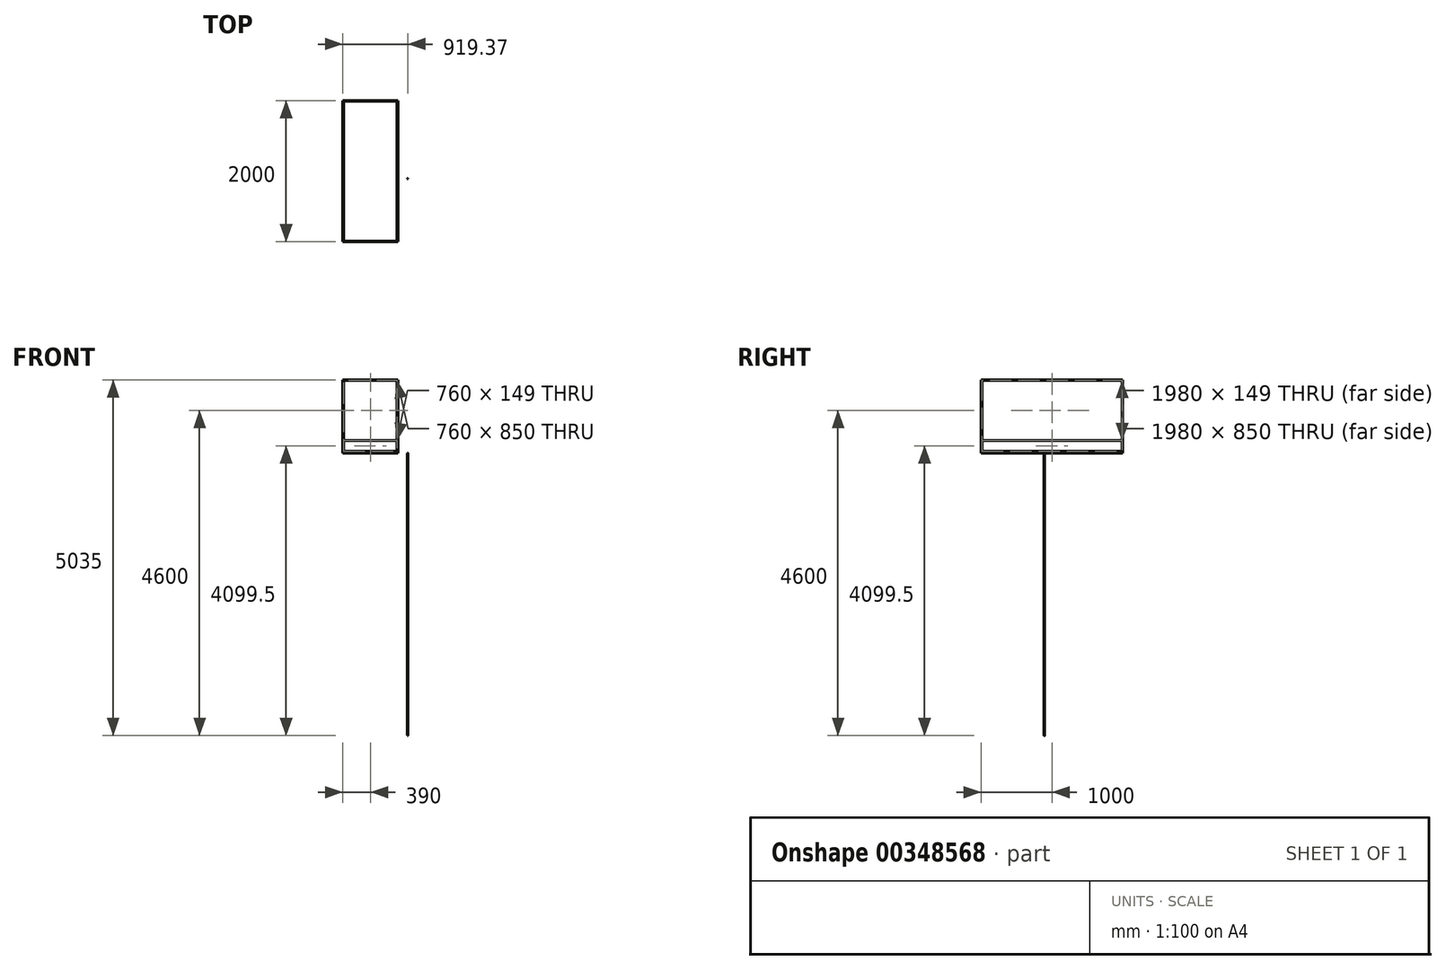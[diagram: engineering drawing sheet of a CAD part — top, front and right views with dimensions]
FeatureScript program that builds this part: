
annotation { "Feature Type Name" : "Feature", "Feature Type Description" : "" }
export const myFeature = defineFeature(function(context is Context, id is Id, definition is map)
    precondition{}
    {
        {
            var Q0;
            Q0=qCreatedBy(makeId("Top.planeOp"),FACE);
            var sketch = newSketch(context, id + "F0", { "sketchPlane" : qUnion([Q0])});
            skLineSegment(sketch, "E0.rect.bottom", {"start": v(390, -1000) * mm, "end": v(-390, -1000) * mm});
            skLineSegment(sketch, "E0.rect.top", {"start": v(390, 1000) * mm, "end": v(-390, 1000) * mm});
            skLineSegment(sketch, "E0.rect.left", {"start": v(390, -1000) * mm, "end": v(390, 1000) * mm});
            skLineSegment(sketch, "E0.rect.right", {"start": v(-390, -1000) * mm, "end": v(-390, 1000) * mm});
            skPoint(sketch, "E0.rect.middle", {"position": v(0, 0) * mm});
            skSolve(sketch);
        }
        {
            var Q0;
            Q0=makeQuery(id+"F0.imprint","IMPRINT",FACE,{"disambiguationData":[TD([[makeQuery(id+"F0.imprint","IMPRINT",EDGE,{"derivedFrom":sQuery(id+"F0.wireOp",EDGE,"E0.rect.bottom")}),-1.0]])]});
            extrude(context, id + "F1", {"entities" : qUnion([Q0]), "depth" : 25 * mm});
        }
        {
            var Q0;
            Q0=makeQuery(id+"F1.opExtrude","CAP_FACE",FACE,{"disambiguationData":[OSD([sQuery(id+"F0.wireOp",EDGE,"E0.rect.bottom"),sQuery(id+"F0.wireOp",EDGE,"E0.rect.top"),sQuery(id+"F0.wireOp",EDGE,"E0.rect.left"),sQuery(id+"F0.wireOp",EDGE,"E0.rect.right")])],"isStart":false});
            var sketch = newSketch(context, id + "F2", { "sketchPlane" : qUnion([Q0])});
            skLineSegment(sketch, "E1.bottom", {"start": v(-390, -1000) * mm, "end": v(-380, -1000) * mm});
            skLineSegment(sketch, "E1.top", {"start": v(-390, -990) * mm, "end": v(-380, -990) * mm});
            skLineSegment(sketch, "E1.left", {"start": v(-390, -1000) * mm, "end": v(-390, -990) * mm});
            skLineSegment(sketch, "E1.right", {"start": v(-380, -1000) * mm, "end": v(-380, -990) * mm});
            skLineSegment(sketch, "E2.bottom", {"start": v(390, -1000) * mm, "end": v(380, -1000) * mm});
            skLineSegment(sketch, "E2.top", {"start": v(390, -990) * mm, "end": v(380, -990) * mm});
            skLineSegment(sketch, "E2.left", {"start": v(390, -1000) * mm, "end": v(390, -990) * mm});
            skLineSegment(sketch, "E2.right", {"start": v(380, -1000) * mm, "end": v(380, -990) * mm});
            skLineSegment(sketch, "E3.bottom", {"start": v(390, 1000) * mm, "end": v(380, 1000) * mm});
            skLineSegment(sketch, "E3.top", {"start": v(390, 990) * mm, "end": v(380, 990) * mm});
            skLineSegment(sketch, "E3.left", {"start": v(390, 1000) * mm, "end": v(390, 990) * mm});
            skLineSegment(sketch, "E3.right", {"start": v(380, 1000) * mm, "end": v(380, 990) * mm});
            skLineSegment(sketch, "E4.bottom", {"start": v(-390, 1000) * mm, "end": v(-380, 1000) * mm});
            skLineSegment(sketch, "E4.top", {"start": v(-390, 990) * mm, "end": v(-380, 990) * mm});
            skLineSegment(sketch, "E4.left", {"start": v(-390, 1000) * mm, "end": v(-390, 990) * mm});
            skLineSegment(sketch, "E4.right", {"start": v(-380, 1000) * mm, "end": v(-380, 990) * mm});
            skSolve(sketch);
        }
        {
            var Q0;
            Q0=qSketchRegion(id+"F2",true);
            extrude(context, id + "F3", {"entities" : qUnion([Q0]), "operationType" : NewBodyOperationType.ADD, "depth" : 1000 * mm});
        }
        {
            var Q0;
            Q0=makeQuery(id+"F3.opExtrude","CAP_FACE",FACE,{"disambiguationData":[OSD([sQuery(id+"F2.wireOp",EDGE,"E1.bottom"),sQuery(id+"F2.wireOp",EDGE,"E1.top"),sQuery(id+"F2.wireOp",EDGE,"E1.left"),sQuery(id+"F2.wireOp",EDGE,"E1.right")])],"isStart":false});
            var sketch = newSketch(context, id + "F4", { "sketchPlane" : qUnion([Q0])});
            skLineSegment(sketch, "E5.bottom", {"start": v(-390, -1000) * mm, "end": v(-380, -1000) * mm});
            skLineSegment(sketch, "E5.top", {"start": v(-390, 1000) * mm, "end": v(-380, 1000) * mm});
            skLineSegment(sketch, "E5.left", {"start": v(-390, -1000) * mm, "end": v(-390, 1000) * mm});
            skLineSegment(sketch, "E5.right", {"start": v(-380, -1000) * mm, "end": v(-380, 1000) * mm});
            skLineSegment(sketch, "E6.bottom", {"start": v(390, -1000) * mm, "end": v(380, -1000) * mm});
            skLineSegment(sketch, "E6.top", {"start": v(390, 1000) * mm, "end": v(380, 1000) * mm});
            skLineSegment(sketch, "E6.left", {"start": v(390, -1000) * mm, "end": v(390, 1000) * mm});
            skLineSegment(sketch, "E6.right", {"start": v(380, -1000) * mm, "end": v(380, 1000) * mm});
            skLineSegment(sketch, "E7.bottom", {"start": v(380, 1000) * mm, "end": v(-380, 1000) * mm});
            skLineSegment(sketch, "E7.top", {"start": v(380, 990) * mm, "end": v(-380, 990) * mm});
            skLineSegment(sketch, "E7.left", {"start": v(380, 1000) * mm, "end": v(380, 990) * mm});
            skLineSegment(sketch, "E7.right", {"start": v(-380, 1000) * mm, "end": v(-380, 990) * mm});
            skLineSegment(sketch, "E8.bottom", {"start": v(380, -1000) * mm, "end": v(-380, -1000) * mm});
            skLineSegment(sketch, "E8.top", {"start": v(380, -990) * mm, "end": v(-380, -990) * mm});
            skLineSegment(sketch, "E8.left", {"start": v(380, -1000) * mm, "end": v(380, -990) * mm});
            skLineSegment(sketch, "E8.right", {"start": v(-380, -1000) * mm, "end": v(-380, -990) * mm});
            skSolve(sketch);
        }
        {
            var Q0;
            Q0=qSketchRegion(id+"F4",true);
            extrude(context, id + "F5", {"entities" : qUnion([Q0]), "operationType" : NewBodyOperationType.ADD, "depth" : 10 * mm});
        }
        {
            var Q0;
            Q0=makeQuery(id+"F1.opExtrude","CAP_FACE",FACE,{"disambiguationData":[OSD([sQuery(id+"F0.wireOp",EDGE,"E0.rect.bottom"),sQuery(id+"F0.wireOp",EDGE,"E0.rect.top"),sQuery(id+"F0.wireOp",EDGE,"E0.rect.left"),sQuery(id+"F0.wireOp",EDGE,"E0.rect.right")])],"isStart":false});
            extrude(context, id + "F6", {"entities" : qUnion([Q0]), "operationType" : NewBodyOperationType.ADD, "depth" : 150 * mm, "hasSecondDirection" : true, "secondDirectionOppositeDirection" : false, "secondDirectionDepth" : 149 * mm});
        }
        {
            var Q0;
            Q0=makeQuery(id+"F1.opExtrude","CAP_FACE",FACE,{"disambiguationData":[OSD([sQuery(id+"F0.wireOp",EDGE,"E0.rect.bottom"),sQuery(id+"F0.wireOp",EDGE,"E0.rect.top"),sQuery(id+"F0.wireOp",EDGE,"E0.rect.left"),sQuery(id+"F0.wireOp",EDGE,"E0.rect.right")])],"isStart":true});
            var sketch = newSketch(context, id + "F7", { "sketchPlane" : qUnion([Q0])});
            skCircle(sketch, "E9", {"center": v(526.87, 106.95) * mm, "radius": 2.5 * mm});
            skSolve(sketch);
        }
        {
            var Q0;
            Q0=makeQuery(id+"F7.imprint","IMPRINT",FACE,{"disambiguationData":[TD([[makeQuery(id+"F7.imprint","IMPRINT",EDGE,{"derivedFrom":sQuery(id+"F7.wireOp",EDGE,"E9")}),1.0]])]});
            extrude(context, id + "F8", {"entities" : qUnion([Q0]), "depth" : 4000 * mm});
        }
        {
            var Q0;
            Q0=qSketchRegion(id+"F7",true);
            extrude(context, id + "F9", {"entities" : qUnion([Q0]), "depth" : 2000 * mm});
        }
    });
